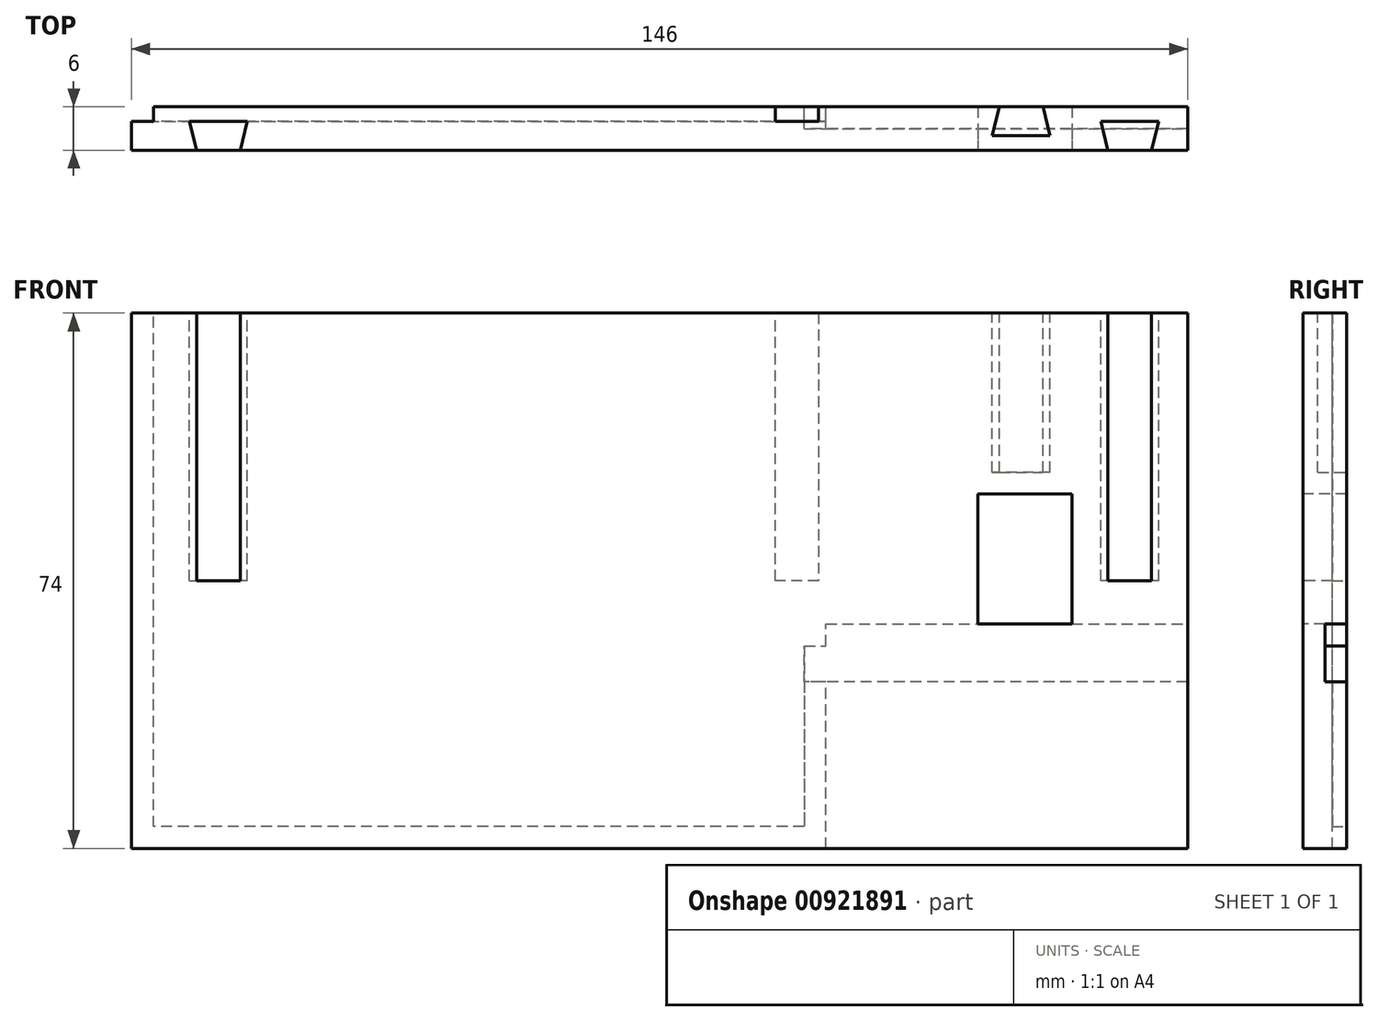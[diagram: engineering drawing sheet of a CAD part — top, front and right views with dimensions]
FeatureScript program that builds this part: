
annotation { "Feature Type Name" : "Feature", "Feature Type Description" : "" }
export const myFeature = defineFeature(function(context is Context, id is Id, definition is map)
    precondition{}
    {
        {
            var Q0;
            Q0=qCreatedBy(makeId("Front.planeOp"),FACE);
            var sketch = newSketch(context, id + "F0", { "sketchPlane" : qUnion([Q0])});
            skLineSegment(sketch, "E0.bottom", {"start": v(0, 0) * mm, "end": v(146, 0) * mm});
            skLineSegment(sketch, "E0.top", {"start": v(0, 74) * mm, "end": v(146, 74) * mm});
            skLineSegment(sketch, "E0.left", {"start": v(0, 0) * mm, "end": v(0, 74) * mm});
            skLineSegment(sketch, "E0.right", {"start": v(146, 0) * mm, "end": v(146, 74) * mm});
            skSolve(sketch);
        }
        {
            var Q0;
            Q0 = qSketchRegion(id + "F0", true);
            var Q1;
            Q1=makeQuery(id+"F0.imprint","IMPRINT",FACE,{"disambiguationData":[TD([[makeQuery(id+"F0.imprint","IMPRINT",EDGE,{"derivedFrom":sQuery(id+"F0.wireOp",EDGE,"E0.bottom")}),1.0]])]});
            extrude(context, id + "F1", {"entities" : qUnion([Q0, Q1]), "depth" : 6 * mm, "offsetDistance" : 25 * mm});
        }
        {
            var Q0;
            Q0=makeQuery(id+"F1.opExtrude","CAP_FACE",FACE,{"disambiguationData":[OSD([sQuery(id+"F0.wireOp",EDGE,"E0.bottom"),sQuery(id+"F0.wireOp",EDGE,"E0.top"),sQuery(id+"F0.wireOp",EDGE,"E0.left"),sQuery(id+"F0.wireOp",EDGE,"E0.right")])],"isStart":false});
            var sketch = newSketch(context, id + "F2", { "sketchPlane" : qUnion([Q0])});
            skLineSegment(sketch, "E1.bottom", {"start": v(117, 31) * mm, "end": v(130, 31) * mm});
            skLineSegment(sketch, "E1.top", {"start": v(117, 49) * mm, "end": v(130, 49) * mm});
            skLineSegment(sketch, "E1.left", {"start": v(117, 31) * mm, "end": v(117, 49) * mm});
            skLineSegment(sketch, "E1.right", {"start": v(130, 31) * mm, "end": v(130, 49) * mm});
            skSolve(sketch);
        }
        {
            var Q0;
            Q0 = qSketchRegion(id + "F2", true);
            var Q1;
            Q1=makeQuery(id+"F2.imprint","IMPRINT",FACE,{"disambiguationData":[TD([[makeQuery(id+"F2.imprint","IMPRINT",EDGE,{"derivedFrom":sQuery(id+"F2.wireOp",EDGE,"E1.bottom")}),1.0]])]});
            extrude(context, id + "F3", {"entities" : qUnion([Q0, Q1]), "operationType" : NewBodyOperationType.REMOVE, "oppositeDirection" : true, "depth" : 6 * mm, "offsetDistance" : 25 * mm});
        }
        {
            var Q0;
            Q0=makeQuery(id+"F1.opExtrude","CAP_FACE",FACE,{"disambiguationData":[OSD([sQuery(id+"F0.wireOp",EDGE,"E0.bottom"),sQuery(id+"F0.wireOp",EDGE,"E0.top"),sQuery(id+"F0.wireOp",EDGE,"E0.left"),sQuery(id+"F0.wireOp",EDGE,"E0.right")])],"isStart":true});
            var sketch = newSketch(context, id + "F4", { "sketchPlane" : qUnion([Q0])});
            skLineSegment(sketch, "E2", {"start": v(-96, 0) * mm, "end": v(-96, 23) * mm});
            skLineSegment(sketch, "E3", {"start": v(-96, 23) * mm, "end": v(-93, 23) * mm});
            skLineSegment(sketch, "E4", {"start": v(-93, 23) * mm, "end": v(-93, 3) * mm});
            skLineSegment(sketch, "E5", {"start": v(-93, 3) * mm, "end": v(-3, 3) * mm});
            skLineSegment(sketch, "E6", {"start": v(-3, 3) * mm, "end": v(-3, 74) * mm});
            skSolve(sketch);
        }
        {
            var Q0;
            {var subQ3=sQuery(id+"F4.wireOp",EDGE,"E2");Q0=makeQuery(id+"F4.imprint","IMPRINT",FACE,{"disambiguationData":[TD([[makeQuery(id+"F4.imprint","IMPRINT",EDGE,{"derivedFrom":subQ3}),-1.0]])]});}
            extrude(context, id + "F5", {"entities" : qUnion([Q0]), "operationType" : NewBodyOperationType.REMOVE, "oppositeDirection" : true, "depth" : 2 * mm, "offsetDistance" : 25 * mm});
        }
        {
            var Q0;
            Q0=makeQuery(id+"F1.opExtrude","CAP_FACE",FACE,{"disambiguationData":[OSD([sQuery(id+"F0.wireOp",EDGE,"E0.bottom"),sQuery(id+"F0.wireOp",EDGE,"E0.top"),sQuery(id+"F0.wireOp",EDGE,"E0.left"),sQuery(id+"F0.wireOp",EDGE,"E0.right")])],"isStart":true});
            var sketch = newSketch(context, id + "F6", { "sketchPlane" : qUnion([Q0])});
            skLineSegment(sketch, "E7", {"start": v(-146, 23) * mm, "end": v(-93, 23) * mm});
            skLineSegment(sketch, "E8", {"start": v(-93, 23) * mm, "end": v(-93, 28) * mm});
            skLineSegment(sketch, "E9", {"start": v(-93, 28) * mm, "end": v(-96, 28) * mm});
            skLineSegment(sketch, "E10", {"start": v(-96, 28) * mm, "end": v(-96, 31) * mm});
            skLineSegment(sketch, "E11", {"start": v(-96, 31) * mm, "end": v(-146, 31) * mm});
            skLineSegment(sketch, "E12", {"start": v(-95, 74) * mm, "end": v(-95, 37) * mm});
            skLineSegment(sketch, "E13", {"start": v(-95, 37) * mm, "end": v(-89, 37) * mm});
            skLineSegment(sketch, "E14", {"start": v(-89, 37) * mm, "end": v(-89, 74) * mm});
            skSolve(sketch);
        }
        {
            var Q0;
            Q0 = qSketchRegion(id + "F6", true);
            var Q1;
            {var subQ0=sQuery(id+"F6.wireOp",EDGE,"E8");Q1=makeQuery(id+"F6.imprint","IMPRINT",FACE,{"disambiguationData":[TD([[makeQuery(id+"F6.imprint","IMPRINT",EDGE,{"derivedFrom":subQ0}),1.0]])]});}
            extrude(context, id + "F7", {"entities" : qUnion([Q0, Q1]), "operationType" : NewBodyOperationType.REMOVE, "oppositeDirection" : true, "depth" : 3 * mm, "offsetDistance" : 25 * mm});
        }
        {
            var Q0;
            {var subQ0=sQuery(id+"F6.wireOp",EDGE,"E12");Q0=makeQuery(id+"F6.imprint","IMPRINT",FACE,{"disambiguationData":[TD([[makeQuery(id+"F6.imprint","IMPRINT",EDGE,{"derivedFrom":subQ0}),1.0]])]});}
            extrude(context, id + "F8", {"entities" : qUnion([Q0]), "operationType" : NewBodyOperationType.REMOVE, "oppositeDirection" : true, "depth" : 2 * mm, "offsetDistance" : 25 * mm});
        }
        {
            var Q0;
            Q0=makeQuery(id+"F1.opExtrude","SWEPT_FACE",FACE,{"disambiguationData":[OSD([sQuery(id+"F0.wireOp",EDGE,"E0.top")])]});
            var sketch = newSketch(context, id + "F9", { "sketchPlane" : qUnion([Q0])});
            skLineSegment(sketch, "E15", {"start": v(142, -6) * mm, "end": v(142, -2) * mm});
            skLineSegment(sketch, "E16", {"start": v(142, -2) * mm, "end": v(134, -2) * mm});
            skLineSegment(sketch, "E17", {"start": v(134, -2) * mm, "end": v(134, -6) * mm});
            skLineSegment(sketch, "E18", {"start": v(8, -6) * mm, "end": v(8, -2) * mm});
            skLineSegment(sketch, "E19", {"start": v(8, -2) * mm, "end": v(16, -2) * mm});
            skLineSegment(sketch, "E20", {"start": v(16, -2) * mm, "end": v(16, -6) * mm});
            skLineSegment(sketch, "E21", {"start": v(127, 0) * mm, "end": v(127, -4) * mm});
            skLineSegment(sketch, "E22", {"start": v(127, -4) * mm, "end": v(119, -4) * mm});
            skLineSegment(sketch, "E23", {"start": v(119, -4) * mm, "end": v(119, 0) * mm});
            skLineSegment(sketch, "E24", {"start": v(142, -2) * mm, "end": v(141, -6) * mm});
            skLineSegment(sketch, "E25", {"start": v(141, -6) * mm, "end": v(142, -6) * mm});
            skLineSegment(sketch, "E26", {"start": v(134, -2) * mm, "end": v(135, -6) * mm});
            skLineSegment(sketch, "E27", {"start": v(135, -6) * mm, "end": v(134, -6) * mm});
            skLineSegment(sketch, "E28", {"start": v(16, -2) * mm, "end": v(15, -6) * mm});
            skLineSegment(sketch, "E29", {"start": v(15, -6) * mm, "end": v(16, -6) * mm});
            skLineSegment(sketch, "E30", {"start": v(8, -2) * mm, "end": v(9, -6) * mm});
            skLineSegment(sketch, "E31", {"start": v(9, -6) * mm, "end": v(8, -6) * mm});
            skLineSegment(sketch, "E32", {"start": v(126, -4) * mm, "end": v(127, -4) * mm});
            skLineSegment(sketch, "E33", {"start": v(120, -4) * mm, "end": v(119, -4) * mm});
            skLineSegment(sketch, "E34", {"start": v(127, -4) * mm, "end": v(126, -4) * mm});
            skLineSegment(sketch, "E35", {"start": v(127, -4) * mm, "end": v(126, 0) * mm});
            skLineSegment(sketch, "E36", {"start": v(126, 0) * mm, "end": v(127, 0) * mm});
            skLineSegment(sketch, "E37", {"start": v(119, -4) * mm, "end": v(120, 0) * mm});
            skLineSegment(sketch, "E38", {"start": v(120, 0) * mm, "end": v(119, 0) * mm});
            skSolve(sketch);
        }
        {
            var Q0;
            Q0=makeQuery(id+"F9.imprint","IMPRINT",FACE,{"disambiguationData":[TD([[makeQuery(id+"F9.imprint","IMPRINT",EDGE,{"derivedFrom":sQuery(id+"F9.wireOp",EDGE,"E16")}),1.0]])]});
            extrude(context, id + "F10", {"entities" : qUnion([Q0]), "operationType" : NewBodyOperationType.REMOVE, "oppositeDirection" : true, "depth" : 37 * mm, "offsetDistance" : 25 * mm});
        }
        {
            var Q0;
            Q0=makeQuery(id+"F9.imprint","IMPRINT",FACE,{"disambiguationData":[TD([[makeQuery(id+"F9.imprint","IMPRINT",EDGE,{"derivedFrom":sQuery(id+"F9.wireOp",EDGE,"E19")}),-1.0]])]});
            extrude(context, id + "F11", {"entities" : qUnion([Q0]), "operationType" : NewBodyOperationType.REMOVE, "oppositeDirection" : true, "depth" : 37 * mm, "offsetDistance" : 25 * mm});
        }
        {
            var Q0;
            {var subQ0=sQuery(id+"F9.wireOp",EDGE,"E35");Q0=makeQuery(id+"F9.imprint","IMPRINT",FACE,{"disambiguationData":[TD([[makeQuery(id+"F9.imprint","IMPRINT",EDGE,{"derivedFrom":subQ0}),1.0]])]});}
            extrude(context, id + "F12", {"entities" : qUnion([Q0]), "operationType" : NewBodyOperationType.REMOVE, "oppositeDirection" : true, "depth" : 22 * mm, "offsetDistance" : 25 * mm});
        }
    });
